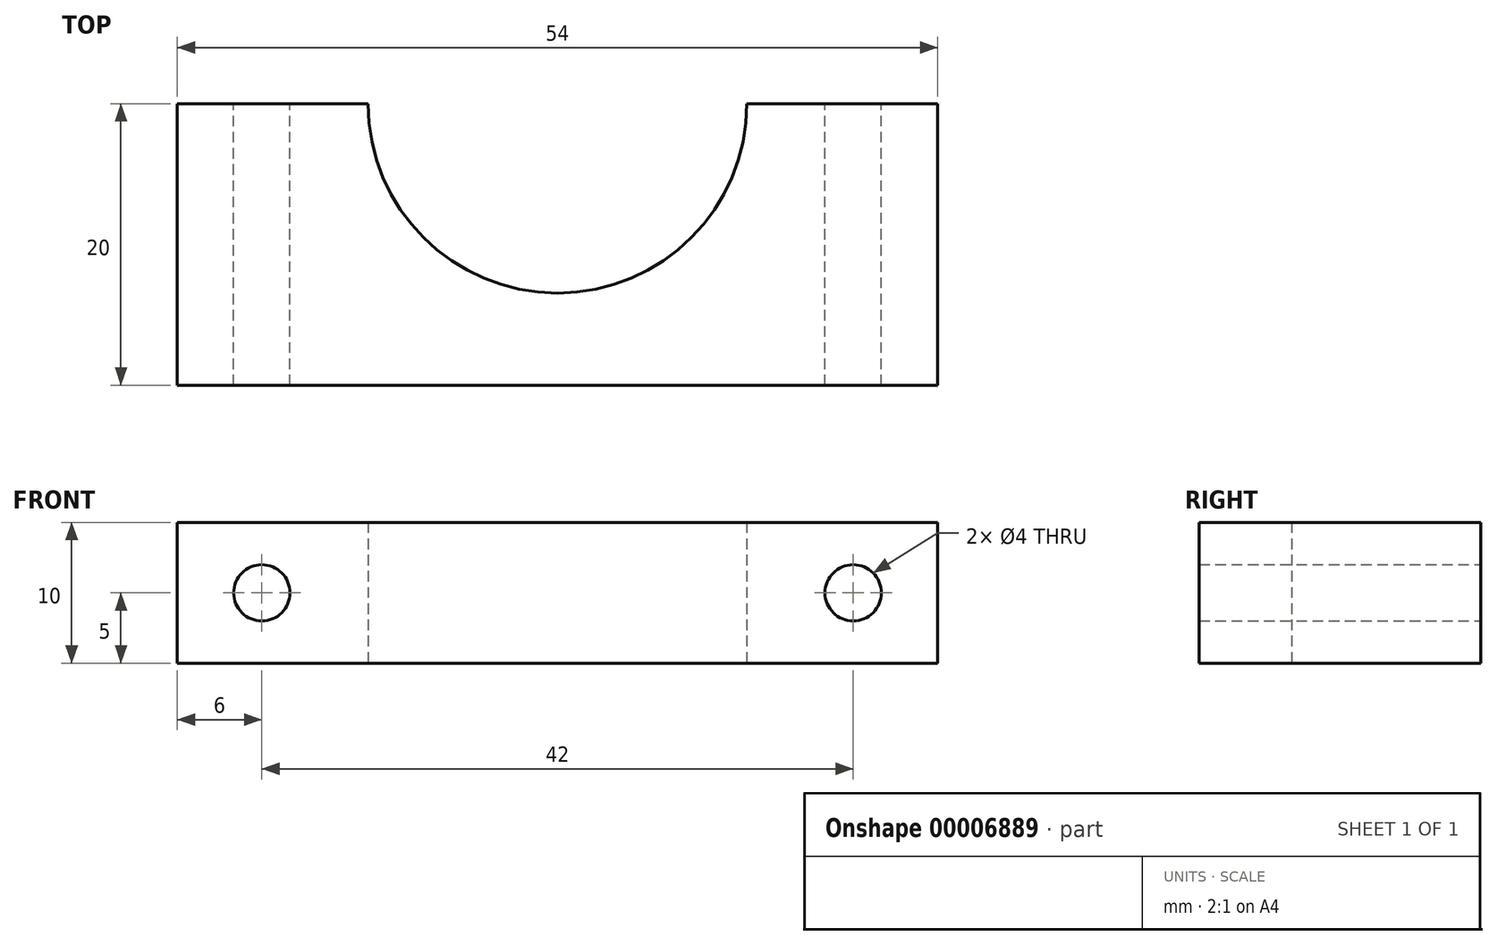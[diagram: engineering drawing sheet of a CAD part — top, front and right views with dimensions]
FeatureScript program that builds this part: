
annotation { "Feature Type Name" : "Feature", "Feature Type Description" : "" }
export const myFeature = defineFeature(function(context is Context, id is Id, definition is map)
    precondition{}
    {
        {
            var Q0;
            Q0=qCreatedBy(makeId("Top.planeOp"),FACE);
            var sketch = newSketch(context, id + "F0", { "sketchPlane" : qUnion([Q0])});
            skLineSegment(sketch, "E0.bottom", {"start": v(-27, -6.56) * mm, "end": v(-13.45, -6.56) * mm});
            skLineSegment(sketch, "E0.top", {"start": v(-27, -26.56) * mm, "end": v(27, -26.56) * mm});
            skLineSegment(sketch, "E0.left", {"start": v(-27, -6.56) * mm, "end": v(-27, -26.56) * mm});
            skLineSegment(sketch, "E0.right", {"start": v(27, -6.56) * mm, "end": v(27, -26.56) * mm});
            skArc(sketch, "E1", {"start": v(-13.45, -6.56) * mm, "mid": v(0, -20.01) * mm, "end": v(13.45, -6.56) * mm});
            skLineSegment(sketch, "E2.trimOffspring", {"start": v(13.45, -6.56) * mm, "end": v(27, -6.56) * mm});
            skSolve(sketch);
        }
        {
            var Q0;
            Q0 = qSketchRegion(id + "F0", true);
            var Q1;
            Q1=makeQuery(id+"F0.imprint","IMPRINT",FACE,{"disambiguationData":[TD([[makeQuery(id+"F0.imprint","IMPRINT",EDGE,{"derivedFrom":sQuery(id+"F0.wireOp",EDGE,"E0.bottom")}),-1.0]])]});
            extrude(context, id + "F1", {"entities" : qUnion([Q0, Q1]), "depth" : 10 * mm});
        }
        {
            var Q0;
            Q0=makeQuery(id+"F1.opExtrude","SWEPT_FACE",FACE,{"disambiguationData":[OSD([sQuery(id+"F0.wireOp",EDGE,"E2.trimOffspring")])]});
            var sketch = newSketch(context, id + "F2", { "sketchPlane" : qUnion([Q0])});
            skLineSegment(sketch, "E3", {"start": v(-21, 10) * mm, "end": v(-21, 0) * mm, "construction": true});
            skLineSegment(sketch, "E4", {"start": v(-27, 5) * mm, "end": v(-13.45, 5) * mm, "construction": true});
            skCircle(sketch, "E5", {"center": v(-21, 5) * mm, "radius": 2 * mm});
            skSolve(sketch);
        }
        {
            var Q0;
            Q0 = qSketchRegion(id + "F2", true);
            extrude(context, id + "F3", {"entities" : qUnion([Q0]), "operationType" : NewBodyOperationType.REMOVE, "endBound" : BoundingType.THROUGH_ALL, "oppositeDirection" : true, "depth" : 25 * mm});
        }
        {
            var Q0;
            Q0=makeQuery(id+"F1.opExtrude","SWEPT_FACE",FACE,{"disambiguationData":[OSD([sQuery(id+"F0.wireOp",EDGE,"E0.bottom")])]});
            var sketch = newSketch(context, id + "F4", { "sketchPlane" : qUnion([Q0])});
            skLineSegment(sketch, "E6", {"start": v(21, 10) * mm, "end": v(21, 0) * mm, "construction": true});
            skLineSegment(sketch, "E7", {"start": v(27, 5) * mm, "end": v(13.45, 5) * mm, "construction": true});
            skCircle(sketch, "E8", {"center": v(21, 5) * mm, "radius": 2 * mm});
            skSolve(sketch);
        }
        {
            var Q0;
            Q0 = qSketchRegion(id + "F4", true);
            extrude(context, id + "F5", {"entities" : qUnion([Q0]), "operationType" : NewBodyOperationType.REMOVE, "endBound" : BoundingType.THROUGH_ALL, "oppositeDirection" : true, "depth" : 25 * mm});
        }
    });
